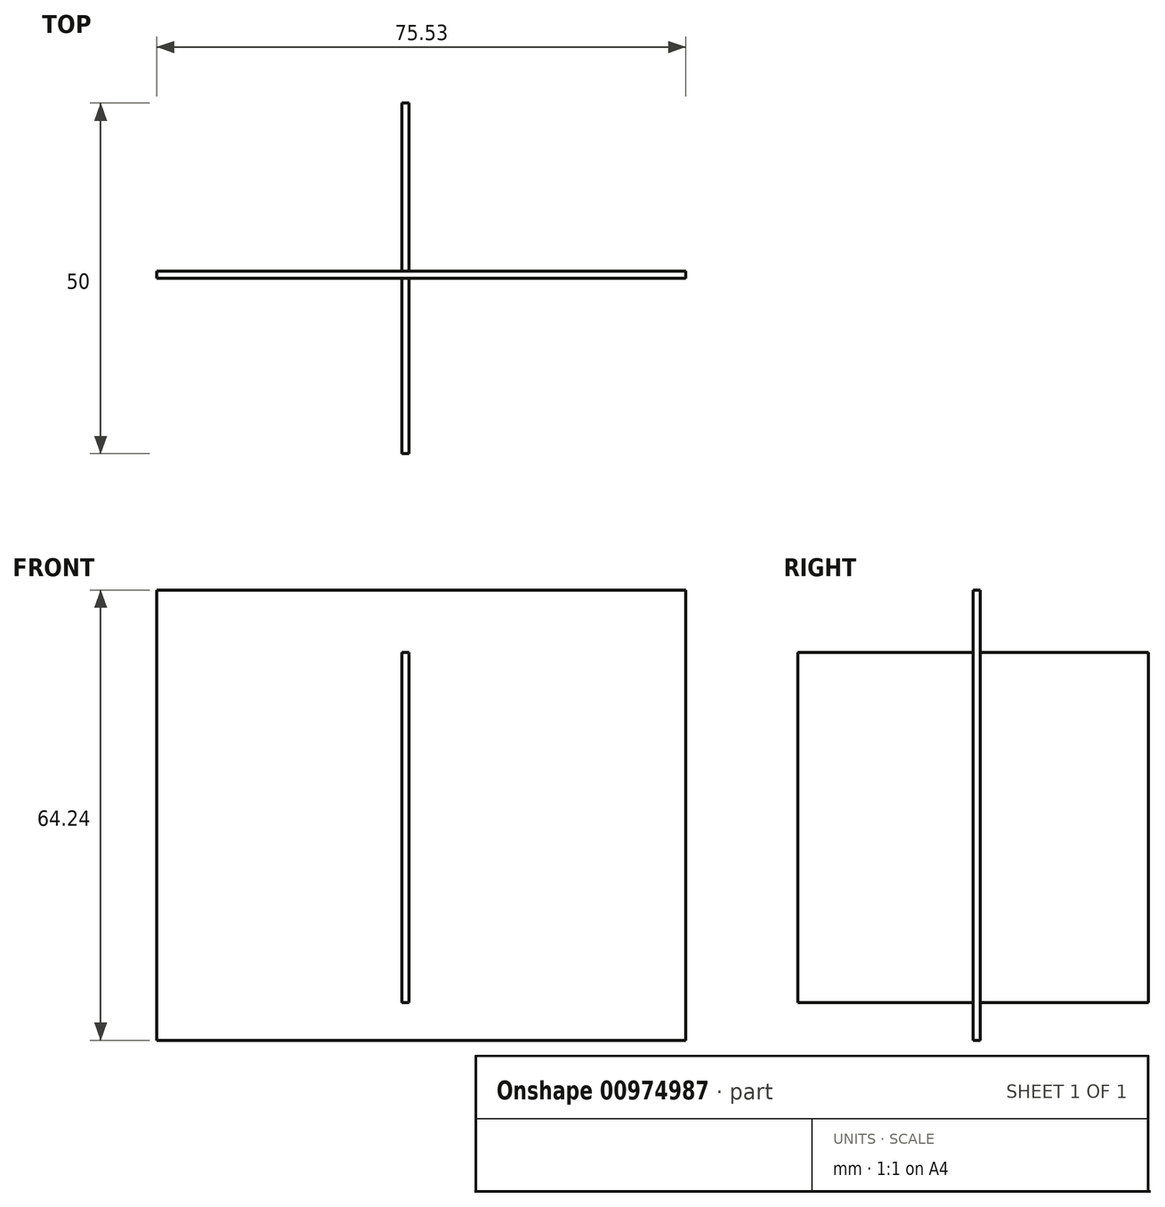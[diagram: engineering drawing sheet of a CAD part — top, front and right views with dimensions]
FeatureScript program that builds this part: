
annotation { "Feature Type Name" : "Feature", "Feature Type Description" : "" }
export const myFeature = defineFeature(function(context is Context, id is Id, definition is map)
    precondition{}
    {
        {
            var Q0;
            Q0=qCreatedBy(makeId("Front.planeOp"),FACE);
            var sketch = newSketch(context, id + "F0", { "sketchPlane" : qUnion([Q0])});
            skLineSegment(sketch, "E0.bottom", {"start": v(-43.18, 48.56) * mm, "end": v(32.35, 48.56) * mm});
            skLineSegment(sketch, "E0.top", {"start": v(-43.18, -15.68) * mm, "end": v(32.35, -15.68) * mm});
            skLineSegment(sketch, "E0.left", {"start": v(-43.18, 48.56) * mm, "end": v(-43.18, -15.68) * mm});
            skLineSegment(sketch, "E0.right", {"start": v(32.35, 48.56) * mm, "end": v(32.35, -15.68) * mm});
            skSolve(sketch);
        }
        {
            var Q0;
            Q0=makeQuery(id+"F0.imprint","IMPRINT",FACE,{"disambiguationData":[TD([[makeQuery(id+"F0.imprint","IMPRINT",EDGE,{"derivedFrom":sQuery(id+"F0.wireOp",EDGE,"E0.bottom")}),-1.0]])]});
            extrude(context, id + "F1", {"entities" : qUnion([Q0]), "depth" : 1 * mm, "offsetDistance" : 25 * mm});
        }
        {
            var Q0;
            Q0=makeQuery(id+"F1.opExtrude","CAP_FACE",FACE,{"disambiguationData":[OSD([sQuery(id+"F0.wireOp",EDGE,"E0.bottom"),sQuery(id+"F0.wireOp",EDGE,"E0.top"),sQuery(id+"F0.wireOp",EDGE,"E0.left"),sQuery(id+"F0.wireOp",EDGE,"E0.right")])],"isStart":false});
            var sketch = newSketch(context, id + "F2", { "sketchPlane" : qUnion([Q0])});
            skLineSegment(sketch, "E1.bottom", {"start": v(-7.19, 39.7) * mm, "end": v(-8.19, 39.7) * mm});
            skLineSegment(sketch, "E1.top", {"start": v(-7.19, -10.3) * mm, "end": v(-8.19, -10.3) * mm});
            skLineSegment(sketch, "E1.left", {"start": v(-7.19, 39.7) * mm, "end": v(-7.19, -10.3) * mm});
            skLineSegment(sketch, "E1.right", {"start": v(-8.19, 39.7) * mm, "end": v(-8.19, -10.3) * mm});
            skPoint(sketch, "E1.middle", {"position": v(-7.69, 14.7) * mm});
            skSolve(sketch);
        }
        {
            var Q0;
            Q0=makeQuery(id+"F2.imprint","IMPRINT",FACE,{"disambiguationData":[TD([[makeQuery(id+"F2.imprint","IMPRINT",EDGE,{"derivedFrom":sQuery(id+"F2.wireOp",EDGE,"E1.bottom")}),1.0]])]});
            extrude(context, id + "F3", {"entities" : qUnion([Q0]), "operationType" : NewBodyOperationType.ADD, "endBound" : BoundingType.SYMMETRIC, "depth" : 50 * mm, "offsetDistance" : 25 * mm});
        }
    });
